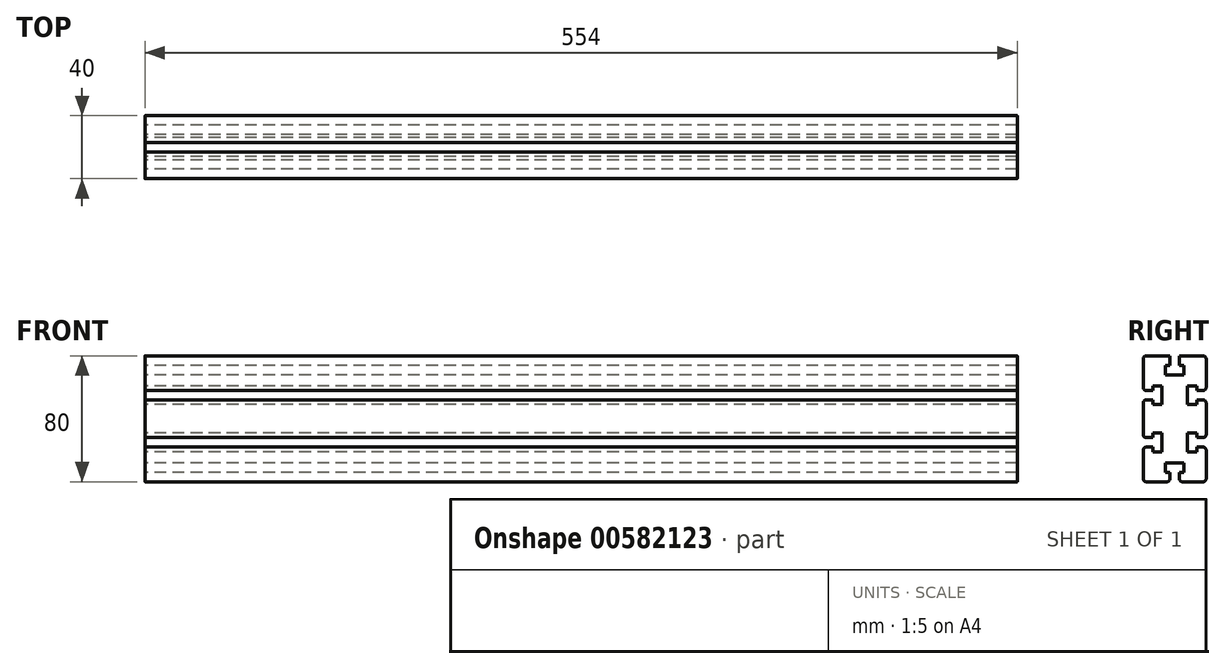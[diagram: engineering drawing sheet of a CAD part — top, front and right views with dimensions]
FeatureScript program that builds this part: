
annotation { "Feature Type Name" : "Feature", "Feature Type Description" : "" }
export const myFeature = defineFeature(function(context is Context, id is Id, definition is map)
    precondition{}
    {
        {
            var Q0;
            Q0=qCreatedBy(makeId("Right.planeOp"),FACE);
            var sketch = newSketch(context, id + "F0", { "sketchPlane" : qUnion([Q0])});
            skLineSegment(sketch, "E0.bottom", {"start": v(-20, 40) * mm, "end": v(-3, 40) * mm});
            skLineSegment(sketch, "E0.top", {"start": v(-20, -40) * mm, "end": v(-3, -40) * mm});
            skLineSegment(sketch, "E0.left", {"start": v(-20, 40) * mm, "end": v(-20, 18) * mm});
            skLineSegment(sketch, "E0.right", {"start": v(20, 40) * mm, "end": v(20, 18) * mm});
            skPoint(sketch, "E0.middle", {"position": v(0, 0) * mm});
            skLineSegment(sketch, "E1.left", {"start": v(-3, 34) * mm, "end": v(-3, 40) * mm});
            skLineSegment(sketch, "E1.right", {"start": v(3, 34) * mm, "end": v(3, 40) * mm});
            skPoint(sketch, "E1.middle", {"position": v(0, 40) * mm});
            skLineSegment(sketch, "E2.bottom", {"start": v(6, 34) * mm, "end": v(3, 34) * mm});
            skLineSegment(sketch, "E2.top", {"start": v(6, 28) * mm, "end": v(-6, 28) * mm});
            skLineSegment(sketch, "E2.left", {"start": v(6, 34) * mm, "end": v(6, 28) * mm});
            skLineSegment(sketch, "E2.right", {"start": v(-6, 34) * mm, "end": v(-6, 28) * mm});
            skPoint(sketch, "E2.middle", {"position": v(0, 31) * mm});
            skPoint(sketch, "E1.top.end.orphan", {"position": v(3, 46) * mm});
            skPoint(sketch, "E3.orphan", {"position": v(-3, 46) * mm});
            skLineSegment(sketch, "E4.trimOffspring", {"start": v(3, 40) * mm, "end": v(20, 40) * mm});
            skLineSegment(sketch, "E5.trimOffspring", {"start": v(-3, 34) * mm, "end": v(-6, 34) * mm});
            skPoint(sketch, "E6.middle", {"position": v(-20, 15) * mm});
            skPoint(sketch, "E7.middle", {"position": v(-11, 15) * mm});
            skLineSegment(sketch, "E8.bottom", {"start": v(-20, -18) * mm, "end": v(-14, -18) * mm});
            skLineSegment(sketch, "E8.top", {"start": v(-20, -12) * mm, "end": v(-14, -12) * mm});
            skPoint(sketch, "E8.middle", {"position": v(-20, -15) * mm});
            skLineSegment(sketch, "E9.bottom", {"start": v(-14, -9) * mm, "end": v(-8, -9) * mm});
            skLineSegment(sketch, "E9.top", {"start": v(-14, -21) * mm, "end": v(-8, -21) * mm});
            skLineSegment(sketch, "E9.left", {"start": v(-14, -9) * mm, "end": v(-14, -12) * mm});
            skLineSegment(sketch, "E9.right", {"start": v(-8, -9) * mm, "end": v(-8, -21) * mm});
            skPoint(sketch, "E9.middle", {"position": v(-11, -15) * mm});
            skPoint(sketch, "E6.left.end.orphan", {"position": v(-14.75, 18) * mm});
            skPoint(sketch, "E6.left.start.orphan", {"position": v(-14.75, 12) * mm});
            skPoint(sketch, "E6.right.end.orphan", {"position": v(-25.25, 18) * mm});
            skPoint(sketch, "E6.right.start.orphan", {"position": v(-25.25, 12) * mm});
            skPoint(sketch, "E7.bottom.start.orphan", {"position": v(-14, 21) * mm});
            skPoint(sketch, "E7.right.start.orphan", {"position": v(-8, 20.4) * mm});
            skPoint(sketch, "E7.top.end.orphan", {"position": v(-8, 9) * mm});
            skPoint(sketch, "E7.top.start.orphan", {"position": v(-14, 9.6) * mm});
            skLineSegment(sketch, "E10.bottom", {"start": v(-14, 18) * mm, "end": v(-20, 18) * mm});
            skLineSegment(sketch, "E10.top", {"start": v(-14, 12) * mm, "end": v(-20, 12) * mm});
            skLineSegment(sketch, "E11.bottom", {"start": v(-14, 21) * mm, "end": v(-8, 21) * mm});
            skLineSegment(sketch, "E11.top", {"start": v(-14, 9) * mm, "end": v(-8, 9) * mm});
            skLineSegment(sketch, "E11.right", {"start": v(-8, 21) * mm, "end": v(-8, 9) * mm});
            skLineSegment(sketch, "E12.bottom", {"start": v(14, 12) * mm, "end": v(20, 12) * mm});
            skLineSegment(sketch, "E12.top", {"start": v(14, 18) * mm, "end": v(20, 18) * mm});
            skPoint(sketch, "E12.middle", {"position": v(20, 15) * mm});
            skLineSegment(sketch, "E13.bottom", {"start": v(14, 21) * mm, "end": v(8, 21) * mm});
            skLineSegment(sketch, "E13.top", {"start": v(14, 9) * mm, "end": v(8, 9) * mm});
            skLineSegment(sketch, "E13.left", {"start": v(14, 21) * mm, "end": v(14, 18) * mm});
            skLineSegment(sketch, "E13.right", {"start": v(8, 21) * mm, "end": v(8, 9) * mm});
            skPoint(sketch, "E13.middle", {"position": v(11, 15) * mm});
            skPoint(sketch, "E13.middle.positionSnap0", {"position": v(14, 15) * mm});
            skPoint(sketch, "E13.centerSnap0", {"position": v(14, 15) * mm});
            skLineSegment(sketch, "E14.bottom", {"start": v(14, -18) * mm, "end": v(20, -18) * mm});
            skLineSegment(sketch, "E14.top", {"start": v(14, -12) * mm, "end": v(20, -12) * mm});
            skPoint(sketch, "E14.middle", {"position": v(20, -15) * mm});
            skLineSegment(sketch, "E15.bottom", {"start": v(14, -9) * mm, "end": v(8, -9) * mm});
            skLineSegment(sketch, "E15.top", {"start": v(14, -21) * mm, "end": v(8, -21) * mm});
            skLineSegment(sketch, "E15.left", {"start": v(14, -9) * mm, "end": v(14, -12) * mm});
            skLineSegment(sketch, "E15.right", {"start": v(8, -9) * mm, "end": v(8, -21) * mm});
            skPoint(sketch, "E15.middle", {"position": v(11, -15) * mm});
            skPoint(sketch, "E15.middle.positionSnap0", {"position": v(14, -15) * mm});
            skPoint(sketch, "E15.centerSnap0", {"position": v(14, -15) * mm});
            skLineSegment(sketch, "E16.left", {"start": v(-3, -34) * mm, "end": v(-3, -40) * mm});
            skLineSegment(sketch, "E16.right", {"start": v(3, -34) * mm, "end": v(3, -40) * mm});
            skPoint(sketch, "E16.middle", {"position": v(0, -40) * mm});
            skLineSegment(sketch, "E17.bottom", {"start": v(6, -34) * mm, "end": v(3, -34) * mm});
            skLineSegment(sketch, "E17.top", {"start": v(6, -28) * mm, "end": v(-6, -28) * mm});
            skLineSegment(sketch, "E17.left", {"start": v(6, -34) * mm, "end": v(6, -28) * mm});
            skLineSegment(sketch, "E17.right", {"start": v(-6, -34) * mm, "end": v(-6, -28) * mm});
            skPoint(sketch, "E17.middle", {"position": v(0, -31) * mm});
            skPoint(sketch, "E17.middle.positionSnap0", {"position": v(0, -34) * mm});
            skPoint(sketch, "E17.centerSnap0", {"position": v(0, -34) * mm});
            skPoint(sketch, "E18.orphan", {"position": v(-28.22, 18) * mm});
            skPoint(sketch, "E19.orphan", {"position": v(-28.22, 12) * mm});
            skLineSegment(sketch, "E20.trimOffspring", {"start": v(-20, 12) * mm, "end": v(-20, -12) * mm});
            skLineSegment(sketch, "E21.trimOffspring", {"start": v(-14, 12) * mm, "end": v(-14, 9) * mm});
            skPoint(sketch, "E22.orphan", {"position": v(-11.78, 18) * mm});
            skPoint(sketch, "E23.orphan", {"position": v(-11.78, 12) * mm});
            skLineSegment(sketch, "E24", {"start": v(-14, 21) * mm, "end": v(-14, 18) * mm});
            skLineSegment(sketch, "E25.trimOffspring", {"start": v(14, 12) * mm, "end": v(14, 9) * mm});
            skPoint(sketch, "E26.orphan", {"position": v(26, 18) * mm});
            skPoint(sketch, "E27.orphan", {"position": v(26, 12) * mm});
            skLineSegment(sketch, "E28.trimOffspring", {"start": v(20, 12) * mm, "end": v(20, -12) * mm});
            skPoint(sketch, "E14.right.end.orphan", {"position": v(26, -12) * mm});
            skPoint(sketch, "E14.right.start.orphan", {"position": v(26, -18) * mm});
            skLineSegment(sketch, "E29.trimOffspring", {"start": v(20, -18) * mm, "end": v(20, -40) * mm});
            skLineSegment(sketch, "E30.trimOffspring", {"start": v(14, -18) * mm, "end": v(14, -21) * mm});
            skLineSegment(sketch, "E31.trimOffspring", {"start": v(-14, -18) * mm, "end": v(-14, -21) * mm});
            skPoint(sketch, "E32.orphan", {"position": v(-26, -12) * mm});
            skPoint(sketch, "E33.orphan", {"position": v(-26, -18) * mm});
            skLineSegment(sketch, "E34.trimOffspring", {"start": v(-20, -18) * mm, "end": v(-20, -40) * mm});
            skLineSegment(sketch, "E35.trimOffspring", {"start": v(-3, -34) * mm, "end": v(-6, -34) * mm});
            skLineSegment(sketch, "E36.trimOffspring", {"start": v(3, -40) * mm, "end": v(20, -40) * mm});
            skPoint(sketch, "E16.top.end.orphan", {"position": v(3, -46) * mm});
            skPoint(sketch, "E37.orphan", {"position": v(-3, -46) * mm});
            skSolve(sketch);
        }
        {
            var Q0;
            Q0=qSketchRegion(id+"F0",true);
            extrude(context, id + "F1", {"entities" : qUnion([Q0]), "depth" : 554 * mm, "offsetDistance" : 25 * mm});
        }
        {
            var Q0;
            Q0=makeQuery(id+"F1.opExtrude","SWEPT_EDGE",EDGE,{"disambiguationData":[OSD([sQuery(id+"F0.wireOp",EDGE,"E0.bottom"),sQuery(id+"F0.wireOp",EDGE,"E0.left")])]});
            var Q1;
            Q1=makeQuery(id+"F1.opExtrude","SWEPT_EDGE",EDGE,{"disambiguationData":[OSD([sQuery(id+"F0.wireOp",EDGE,"E0.left"),sQuery(id+"F0.wireOp",EDGE,"E10.bottom")])]});
            var Q2;
            Q2=makeQuery(id+"F1.opExtrude","SWEPT_EDGE",EDGE,{"disambiguationData":[OSD([sQuery(id+"F0.wireOp",EDGE,"E10.top"),sQuery(id+"F0.wireOp",EDGE,"E20.trimOffspring")])]});
            var Q3;
            Q3=makeQuery(id+"F1.opExtrude","SWEPT_EDGE",EDGE,{"disambiguationData":[OSD([sQuery(id+"F0.wireOp",EDGE,"E8.top"),sQuery(id+"F0.wireOp",EDGE,"E20.trimOffspring")])]});
            var Q4;
            Q4=makeQuery(id+"F1.opExtrude","SWEPT_EDGE",EDGE,{"disambiguationData":[OSD([sQuery(id+"F0.wireOp",EDGE,"E8.bottom"),sQuery(id+"F0.wireOp",EDGE,"E34.trimOffspring")])]});
            var Q5;
            Q5=makeQuery(id+"F1.opExtrude","SWEPT_EDGE",EDGE,{"disambiguationData":[OSD([sQuery(id+"F0.wireOp",EDGE,"E0.top"),sQuery(id+"F0.wireOp",EDGE,"E34.trimOffspring")])]});
            var Q6;
            Q6=makeQuery(id+"F1.opExtrude","SWEPT_EDGE",EDGE,{"disambiguationData":[OSD([sQuery(id+"F0.wireOp",EDGE,"E0.top"),sQuery(id+"F0.wireOp",EDGE,"E16.left")])]});
            var Q7;
            Q7=makeQuery(id+"F1.opExtrude","SWEPT_EDGE",EDGE,{"disambiguationData":[OSD([sQuery(id+"F0.wireOp",EDGE,"E16.right"),sQuery(id+"F0.wireOp",EDGE,"E36.trimOffspring")])]});
            var Q8;
            Q8=makeQuery(id+"F1.opExtrude","SWEPT_EDGE",EDGE,{"disambiguationData":[OSD([sQuery(id+"F0.wireOp",EDGE,"E29.trimOffspring"),sQuery(id+"F0.wireOp",EDGE,"E36.trimOffspring")])]});
            var Q9;
            Q9=makeQuery(id+"F1.opExtrude","SWEPT_EDGE",EDGE,{"disambiguationData":[OSD([sQuery(id+"F0.wireOp",EDGE,"E14.bottom"),sQuery(id+"F0.wireOp",EDGE,"E29.trimOffspring")])]});
            var Q10;
            Q10=makeQuery(id+"F1.opExtrude","SWEPT_EDGE",EDGE,{"disambiguationData":[OSD([sQuery(id+"F0.wireOp",EDGE,"E12.bottom"),sQuery(id+"F0.wireOp",EDGE,"E28.trimOffspring")])]});
            var Q11;
            Q11=makeQuery(id+"F1.opExtrude","SWEPT_EDGE",EDGE,{"disambiguationData":[OSD([sQuery(id+"F0.wireOp",EDGE,"E14.top"),sQuery(id+"F0.wireOp",EDGE,"E28.trimOffspring")])]});
            var Q12;
            Q12=makeQuery(id+"F1.opExtrude","SWEPT_EDGE",EDGE,{"disambiguationData":[OSD([sQuery(id+"F0.wireOp",EDGE,"E0.right"),sQuery(id+"F0.wireOp",EDGE,"E4.trimOffspring")])]});
            var Q13;
            Q13=makeQuery(id+"F1.opExtrude","SWEPT_EDGE",EDGE,{"disambiguationData":[OSD([sQuery(id+"F0.wireOp",EDGE,"E0.right"),sQuery(id+"F0.wireOp",EDGE,"E12.top")])]});
            fillet(context, id + "F2", {"entities" : qUnion([Q0, Q1, Q2, Q3, Q4, Q5, Q6, Q7, Q8, Q9, Q10, Q11, Q12, Q13]), "radius" : 2 * mm, "tangentPropagation" : true, "allowEdgeOverflow" : false});
        }
    });
